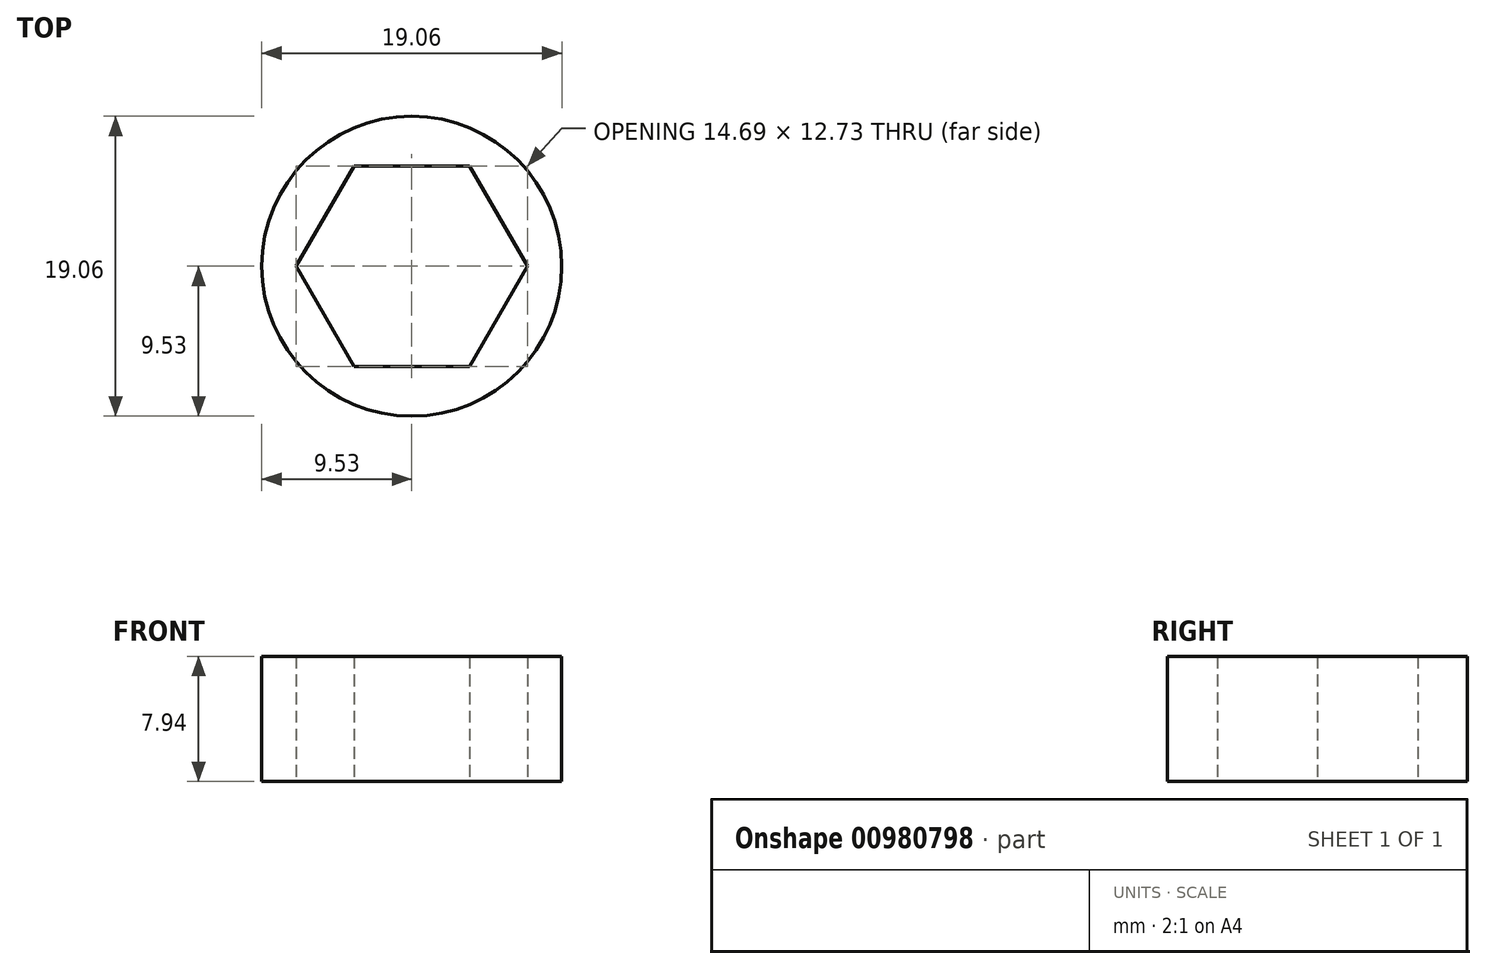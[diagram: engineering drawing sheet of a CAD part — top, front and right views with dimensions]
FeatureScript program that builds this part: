
annotation { "Feature Type Name" : "Feature", "Feature Type Description" : "" }
export const myFeature = defineFeature(function(context is Context, id is Id, definition is map)
    precondition{}
    {
        {
            var Q0;
            Q0=qCreatedBy(makeId("Top.planeOp"),FACE);
            var sketch = newSketch(context, id + "F0", { "sketchPlane" : qUnion([Q0])});
            skCircle(sketch, "E0", {"center": v(0, 0) * mm, "radius": 9.53 * mm});
            skCircle(sketch, "E1.cCircle", {"center": v(0, 0) * mm, "radius": 6.36 * mm, "construction": true});
            skLineSegment(sketch, "E1.0", {"start": v(-3.67, 6.36) * mm, "end": v(3.67, 6.36) * mm});
            skLineSegment(sketch, "E1.1", {"start": v(3.67, 6.36) * mm, "end": v(7.35, 0) * mm});
            skLineSegment(sketch, "E1.2", {"start": v(7.35, 0) * mm, "end": v(3.67, -6.36) * mm});
            skLineSegment(sketch, "E1.3", {"start": v(3.67, -6.36) * mm, "end": v(-3.67, -6.36) * mm});
            skLineSegment(sketch, "E1.4", {"start": v(-3.67, -6.36) * mm, "end": v(-7.35, 0) * mm});
            skLineSegment(sketch, "E1.5", {"start": v(-7.35, 0) * mm, "end": v(-3.67, 6.36) * mm});
            skPoint(sketch, "E1.0.midPoint", {"position": v(0, 6.36) * mm});
            skSolve(sketch);
        }
        {
            var Q0;
            Q0=qSketchRegion(id+"F0",true);
            extrude(context, id + "F1", {"entities" : qUnion([Q0]), "depth" : 7.94 * mm, "offsetDistance" : 25.4 * mm});
        }
    });
